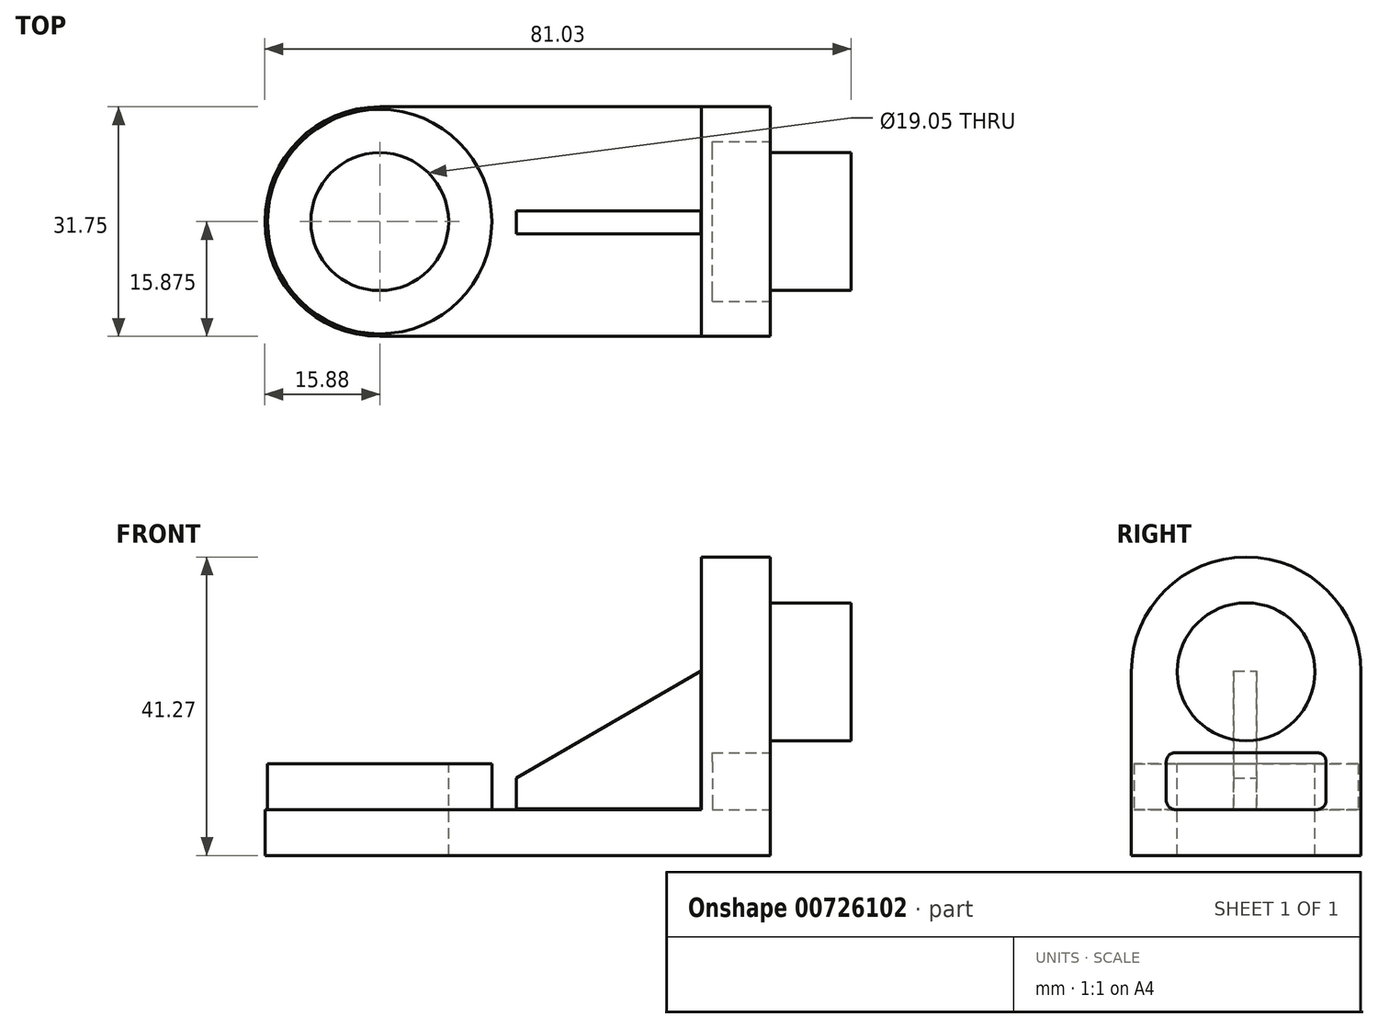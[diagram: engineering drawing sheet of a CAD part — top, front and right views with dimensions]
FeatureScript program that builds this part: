
annotation { "Feature Type Name" : "Feature", "Feature Type Description" : "" }
export const myFeature = defineFeature(function(context is Context, id is Id, definition is map)
    precondition{}
    {
        {
            var Q0;
            Q0=qCreatedBy(makeId("Top.planeOp"),FACE);
            var sketch = newSketch(context, id + "F0", { "sketchPlane" : qUnion([Q0])});
            skLineSegment(sketch, "E0.bottom", {"start": v(0, 0) * mm, "end": v(53.98, 0) * mm});
            skLineSegment(sketch, "E0.top", {"start": v(0, 31.75) * mm, "end": v(53.98, 31.75) * mm});
            skLineSegment(sketch, "E0.left", {"start": v(0, 0) * mm, "end": v(0, 31.75) * mm});
            skLineSegment(sketch, "E0.right", {"start": v(53.98, 0) * mm, "end": v(53.98, 31.75) * mm});
            skArc(sketch, "E1", {"start": v(0, 31.75) * mm, "mid": v(-15.88, 15.87) * mm, "end": v(0, 0) * mm});
            skSolve(sketch);
        }
        {
            var Q0;
            Q0=makeQuery(id+"F0.imprint","IMPRINT",FACE,{"disambiguationData":[TD([[makeQuery(id+"F0.imprint","IMPRINT",EDGE,{"derivedFrom":sQuery(id+"F0.wireOp",EDGE,"E0.left")}),1.0]])]});
            var Q1;
            Q1=makeQuery(id+"F0.imprint","IMPRINT",FACE,{"disambiguationData":[TD([[makeQuery(id+"F0.imprint","IMPRINT",EDGE,{"derivedFrom":sQuery(id+"F0.wireOp",EDGE,"E0.bottom")}),1.0]])]});
            extrude(context, id + "F1", {"entities" : qUnion([Q0, Q1]), "depth" : 6.35 * mm, "offsetDistance" : 25.4 * mm});
        }
        {
            var Q0;
            Q0=makeQuery(id+"F1.opExtrude","CAP_FACE",FACE,{"disambiguationData":[OSD([sQuery(id+"F0.wireOp",EDGE,"E0.bottom"),sQuery(id+"F0.wireOp",EDGE,"E0.top"),sQuery(id+"F0.wireOp",EDGE,"E0.right"),sQuery(id+"F0.wireOp",EDGE,"E1")])],"isStart":false});
            var sketch = newSketch(context, id + "F2", { "sketchPlane" : qUnion([Q0])});
            skCircle(sketch, "E2", {"center": v(0, 15.87) * mm, "radius": 15.5 * mm});
            skSolve(sketch);
        }
        {
            var Q0;
            Q0=makeQuery(id+"F2.imprint","IMPRINT",FACE,{"disambiguationData":[TD([[makeQuery(id+"F2.imprint","IMPRINT",EDGE,{"derivedFrom":sQuery(id+"F2.wireOp",EDGE,"E2")}),1.0]])]});
            extrude(context, id + "F3", {"entities" : qUnion([Q0]), "operationType" : NewBodyOperationType.ADD, "depth" : 6.35 * mm, "offsetDistance" : 25.4 * mm});
        }
        {
            var Q0;
            Q0=makeQuery(id+"F3.opExtrude","CAP_FACE",FACE,{"disambiguationData":[OSD([sQuery(id+"F2.wireOp",EDGE,"E2")])],"isStart":false});
            var sketch = newSketch(context, id + "F4", { "sketchPlane" : qUnion([Q0])});
            skCircle(sketch, "E3", {"center": v(0, 15.87) * mm, "radius": 9.53 * mm});
            skSolve(sketch);
        }
        {
            var Q0;
            Q0=makeQuery(id+"F4.imprint","IMPRINT",FACE,{"disambiguationData":[TD([[makeQuery(id+"F4.imprint","IMPRINT",EDGE,{"derivedFrom":sQuery(id+"F4.wireOp",EDGE,"E3")}),1.0]])]});
            var Q1;
            Q1=sQuery(id+"F4.wireOp",EDGE,"E3");
            extrude(context, id + "F5", {"entities" : qUnion([Q0]), "operationType" : NewBodyOperationType.REMOVE, "surfaceEntities" : qUnion([Q1]), "oppositeDirection" : true, "depth" : 12.7 * mm, "offsetDistance" : 25.4 * mm});
        }
        {
            var Q0;
            Q0=makeQuery(id+"F1.opExtrude","SWEPT_FACE",FACE,{"disambiguationData":[OSD([sQuery(id+"F0.wireOp",EDGE,"E0.bottom")])]});
            var sketch = newSketch(context, id + "F6", { "sketchPlane" : qUnion([Q0])});
            skLineSegment(sketch, "E4.bottom", {"start": v(53.98, 0) * mm, "end": v(44.45, 0) * mm});
            skLineSegment(sketch, "E4.top", {"start": v(53.98, 25.4) * mm, "end": v(44.45, 25.4) * mm});
            skLineSegment(sketch, "E4.left", {"start": v(53.98, 0) * mm, "end": v(53.98, 25.4) * mm});
            skLineSegment(sketch, "E4.right", {"start": v(44.45, 0) * mm, "end": v(44.45, 25.4) * mm});
            skSolve(sketch);
        }
        {
            var Q0;
            {var subQ0=sQuery(id+"F6.wireOp",EDGE,"E4.top");Q0=makeQuery(id+"F6.imprint","IMPRINT",FACE,{"disambiguationData":[TD([[makeQuery(id+"F6.imprint","IMPRINT",EDGE,{"derivedFrom":subQ0}),1.0]])]});}
            extrude(context, id + "F7", {"entities" : qUnion([Q0]), "operationType" : NewBodyOperationType.ADD, "oppositeDirection" : true, "depth" : 31.75 * mm, "offsetDistance" : 25.4 * mm});
        }
        {
            var Q0;
            Q0=makeQuery(id+"F7.boolean.opBoolean","MERGE",FACE,{"derivedFrom":[makeQuery(id+"F1.opExtrude","SWEPT_FACE",FACE,{"disambiguationData":[OSD([sQuery(id+"F0.wireOp",EDGE,"E0.right")])]}),makeQuery(id+"F7.opExtrude","SWEPT_FACE",FACE,{"disambiguationData":[OSD([sQuery(id+"F6.wireOp",EDGE,"E4.left")])]})]});
            var sketch = newSketch(context, id + "F8", { "sketchPlane" : qUnion([Q0])});
            skArc(sketch, "E5", {"start": v(31.75, 25.4) * mm, "mid": v(15.87, 41.28) * mm, "end": v(0, 25.4) * mm});
            skSolve(sketch);
        }
        {
            var Q0;
            Q0=makeQuery(id+"F8.imprint","IMPRINT",FACE,{"disambiguationData":[TD([[makeQuery(id+"F8.imprint","IMPRINT",EDGE,{"derivedFrom":sQuery(id+"F8.wireOp",EDGE,"E5")}),1.0]])]});
            extrude(context, id + "F9", {"entities" : qUnion([Q0]), "operationType" : NewBodyOperationType.ADD, "oppositeDirection" : true, "depth" : 9.52 * mm, "offsetDistance" : 25.4 * mm});
        }
        {
            var Q0;
            {var subQ0=sQuery(id+"F6.wireOp",EDGE,"E4.left");Q0=makeQuery(id+"F9.boolean.opBoolean","MERGE",FACE,{"derivedFrom":[makeQuery(id+"F7.boolean.opBoolean","MERGE",FACE,{"derivedFrom":[makeQuery(id+"F1.opExtrude","SWEPT_FACE",FACE,{"disambiguationData":[OSD([sQuery(id+"F0.wireOp",EDGE,"E0.right")])]}),makeQuery(id+"F7.opExtrude","SWEPT_FACE",FACE,{"disambiguationData":[OSD([subQ0])]})]}),makeQuery(id+"F9.opExtrude","CAP_FACE",FACE,{"disambiguationData":[OSD([sQuery(id+"F6.wireOp",EDGE,"E4.top"),subQ0,sQuery(id+"F8.wireOp",EDGE,"E5")])],"isStart":true})]});}
            var sketch = newSketch(context, id + "F10", { "sketchPlane" : qUnion([Q0])});
            skCircle(sketch, "E6", {"center": v(15.88, 25.4) * mm, "radius": 9.53 * mm});
            skSolve(sketch);
        }
        {
            var Q0;
            Q0=makeQuery(id+"F10.imprint","IMPRINT",FACE,{"disambiguationData":[TD([[makeQuery(id+"F10.imprint","IMPRINT",EDGE,{"derivedFrom":sQuery(id+"F10.wireOp",EDGE,"E6")}),1.0]])]});
            extrude(context, id + "F11", {"entities" : qUnion([Q0]), "operationType" : NewBodyOperationType.ADD, "depth" : 11.18 * mm, "offsetDistance" : 25.4 * mm});
        }
        {
            var Q0;
            {var subQ0=sQuery(id+"F6.wireOp",EDGE,"E4.left");Q0=makeQuery(id+"F9.boolean.opBoolean","MERGE",FACE,{"derivedFrom":[makeQuery(id+"F7.boolean.opBoolean","MERGE",FACE,{"derivedFrom":[makeQuery(id+"F1.opExtrude","SWEPT_FACE",FACE,{"disambiguationData":[OSD([sQuery(id+"F0.wireOp",EDGE,"E0.right")])]}),makeQuery(id+"F7.opExtrude","SWEPT_FACE",FACE,{"disambiguationData":[OSD([subQ0])]})]}),makeQuery(id+"F9.opExtrude","CAP_FACE",FACE,{"disambiguationData":[OSD([sQuery(id+"F6.wireOp",EDGE,"E4.top"),subQ0,sQuery(id+"F8.wireOp",EDGE,"E5")])],"isStart":true})]});}
            var sketch = newSketch(context, id + "F12", { "sketchPlane" : qUnion([Q0])});
            skLineSegment(sketch, "E7.bottom", {"start": v(6.1, 14.22) * mm, "end": v(25.65, 14.22) * mm});
            skLineSegment(sketch, "E7.top", {"start": v(6.1, 6.35) * mm, "end": v(25.65, 6.35) * mm});
            skLineSegment(sketch, "E7.left", {"start": v(4.83, 12.95) * mm, "end": v(4.83, 7.62) * mm});
            skLineSegment(sketch, "E7.right", {"start": v(26.92, 12.95) * mm, "end": v(26.92, 7.62) * mm});
            skPoint(sketch, "E8.visualSharp", {"position": v(4.83, 14.22) * mm});
            skArc(sketch, "E8.filletArc", {"start": v(6.1, 14.22) * mm, "mid": v(5.2, 13.85) * mm, "end": v(4.83, 12.95) * mm});
            skPoint(sketch, "E9.visualSharp", {"position": v(4.83, 6.35) * mm});
            skArc(sketch, "E9.filletArc", {"start": v(4.83, 7.62) * mm, "mid": v(5.2, 6.72) * mm, "end": v(6.1, 6.35) * mm});
            skPoint(sketch, "E10.visualSharp", {"position": v(26.92, 6.35) * mm});
            skArc(sketch, "E10.filletArc", {"start": v(25.65, 6.35) * mm, "mid": v(26.55, 6.72) * mm, "end": v(26.92, 7.62) * mm});
            skPoint(sketch, "E11.visualSharp", {"position": v(26.92, 14.22) * mm});
            skArc(sketch, "E11.filletArc", {"start": v(26.92, 12.95) * mm, "mid": v(26.55, 13.85) * mm, "end": v(25.65, 14.22) * mm});
            skSolve(sketch);
        }
        {
            var Q0;
            Q0=makeQuery(id+"F12.imprint","IMPRINT",FACE,{"disambiguationData":[TD([[makeQuery(id+"F12.imprint","IMPRINT",EDGE,{"derivedFrom":sQuery(id+"F12.wireOp",EDGE,"E7.bottom")}),-1.0]])]});
            extrude(context, id + "F13", {"entities" : qUnion([Q0]), "operationType" : NewBodyOperationType.REMOVE, "oppositeDirection" : true, "depth" : 8 * mm, "offsetDistance" : 25.4 * mm});
        }
        {
            var Q0;
            {var subQ0=sQuery(id+"F0.wireOp",EDGE,"E0.bottom");Q0=makeQuery(id+"F7.boolean.opBoolean","MERGE",FACE,{"derivedFrom":[makeQuery(id+"F1.opExtrude","SWEPT_FACE",FACE,{"disambiguationData":[OSD([subQ0])]}),makeQuery(id+"F7.opExtrude","CAP_FACE",FACE,{"disambiguationData":[OSD([subQ0,sQuery(id+"F6.wireOp",EDGE,"E4.top"),sQuery(id+"F6.wireOp",EDGE,"E4.left"),sQuery(id+"F6.wireOp",EDGE,"E4.right")])],"isStart":true})]});}
            cPlane(context, id + "F14", {"entities" : qUnion([Q0]), "cplaneType" : CPlaneType.OFFSET, "offset" : 15.75 * mm, "oppositeDirection" : true, "width" : 152.4 * mm, "height" : 152.4 * mm});
        }
        {
            var Q0;
            Q0=qCreatedBy(id+"F14.planeOp",FACE);
            var sketch = newSketch(context, id + "F15", { "sketchPlane" : qUnion([Q0])});
            skLineSegment(sketch, "E12", {"start": v(44.43, 25.48) * mm, "end": v(18.86, 10.72) * mm});
            skLineSegment(sketch, "E13", {"start": v(44.43, 6.43) * mm, "end": v(44.43, 25.48) * mm});
            skArc(sketch, "E14", {"start": v(18.86, 10.72) * mm, "mid": v(17.11, 10.43) * mm, "end": v(15.6, 11.35) * mm});
            skLineSegment(sketch, "E15", {"start": v(15.6, 11.35) * mm, "end": v(15.6, 6.43) * mm});
            skLineSegment(sketch, "E16", {"start": v(15.6, 6.43) * mm, "end": v(44.43, 6.43) * mm});
            skLineSegment(sketch, "E17", {"start": v(18.86, 10.72) * mm, "end": v(18.86, 6.43) * mm});
            skSolve(sketch);
        }
        {
            var Q0;
            Q0=makeQuery(id+"F15.imprint","IMPRINT",FACE,{"disambiguationData":[TD([[makeQuery(id+"F15.imprint","IMPRINT",EDGE,{"derivedFrom":sQuery(id+"F15.wireOp",EDGE,"E12")}),1.0]])]});
            extrude(context, id + "F16", {"entities" : qUnion([Q0]), "endBound" : BoundingType.SYMMETRIC, "depth" : 3.17 * mm, "offsetDistance" : 25.4 * mm});
        }
        {
            var Q0;
            Q0=makeQuery(id+"F3.opExtrude","CAP_FACE",FACE,{"disambiguationData":[OSD([sQuery(id+"F2.wireOp",EDGE,"E2")])],"isStart":false});
            var sketch = newSketch(context, id + "F17", { "sketchPlane" : qUnion([Q0])});
            skLineSegment(sketch, "E18", {"start": v(18.94, 17.38) * mm, "end": v(15.43, 17.38) * mm});
            skLineSegment(sketch, "E19", {"start": v(18.94, 14.16) * mm, "end": v(15.41, 14.16) * mm});
            skLineSegment(sketch, "E20", {"start": v(18.94, 17.38) * mm, "end": v(18.94, 14.16) * mm});
            skSolve(sketch);
        }
        {
            var Q0;
            {var subQ0=sQuery(id+"F17.wireOp",EDGE,"E18");Q0=makeQuery(id+"F17.imprint","IMPRINT",FACE,{"disambiguationData":[TD([[makeQuery(id+"F17.imprint","IMPRINT",EDGE,{"derivedFrom":subQ0}),1.0]])]});}
            var Q1;
            Q1=sQuery(id+"F17.wireOp",EDGE,"E18");
            var Q2;
            Q2=sQuery(id+"F17.wireOp",EDGE,"E20");
            var Q3;
            Q3=sQuery(id+"F17.wireOp",EDGE,"E19");
            extrude(context, id + "F18", {"entities" : qUnion([Q0]), "bodyType" : ToolBodyType.SURFACE, "surfaceEntities" : qUnion([Q1, Q2, Q3]), "oppositeDirection" : true, "depth" : 7.57 * mm, "offsetDistance" : 25.4 * mm});
        }
    });
